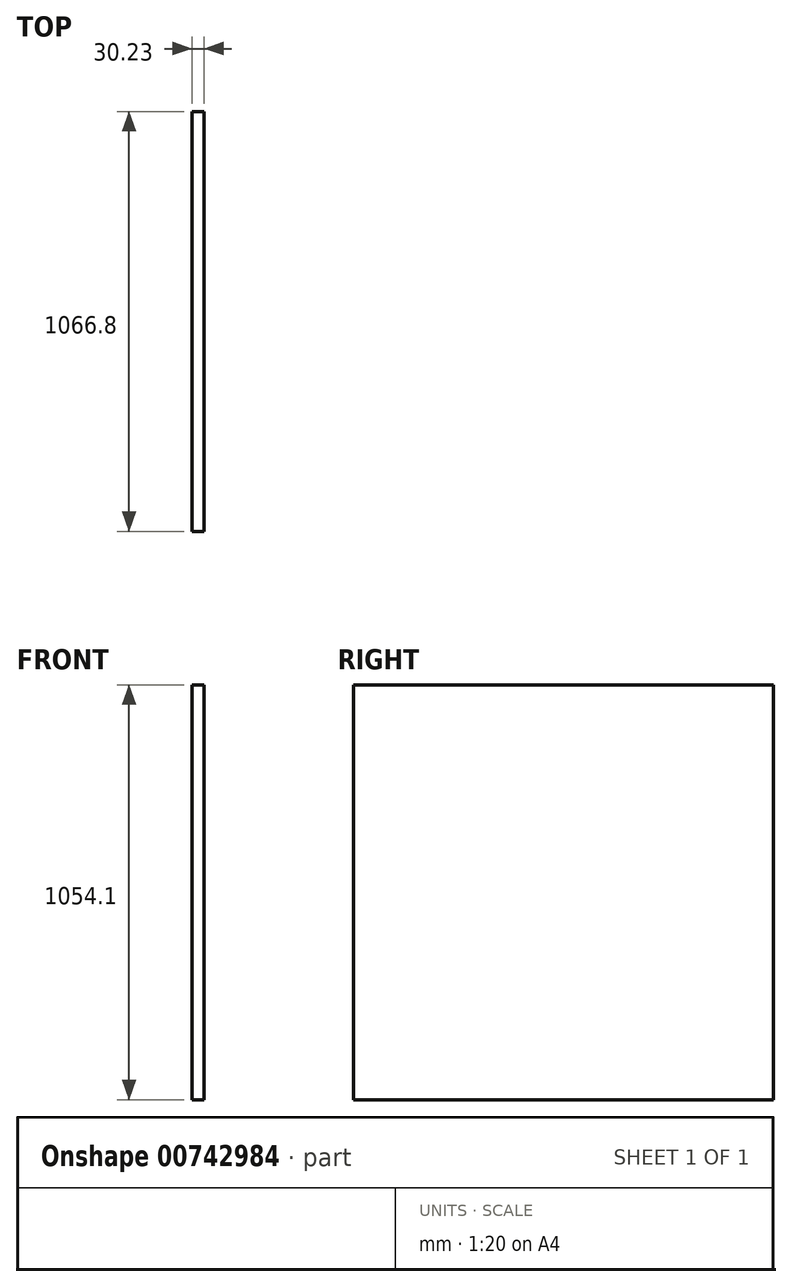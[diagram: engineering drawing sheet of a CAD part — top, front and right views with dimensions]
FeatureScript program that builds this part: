
annotation { "Feature Type Name" : "Feature", "Feature Type Description" : "" }
export const myFeature = defineFeature(function(context is Context, id is Id, definition is map)
    precondition{}
    {
        {
            var Q0;
            Q0=qCreatedBy(makeId("Right.planeOp"),FACE);
            var sketch = newSketch(context, id + "F0", { "sketchPlane" : qUnion([Q0])});
            skLineSegment(sketch, "E0.bottom", {"start": v(533.4, 527.05) * mm, "end": v(-533.4, 527.05) * mm});
            skLineSegment(sketch, "E0.top", {"start": v(533.4, -527.05) * mm, "end": v(-533.4, -527.05) * mm});
            skLineSegment(sketch, "E0.left", {"start": v(533.4, 527.05) * mm, "end": v(533.4, -527.05) * mm});
            skLineSegment(sketch, "E0.right", {"start": v(-533.4, 527.05) * mm, "end": v(-533.4, -527.05) * mm});
            skPoint(sketch, "E0.middle", {"position": v(0, 0) * mm});
            skSolve(sketch);
        }
        {
            var Q0;
            Q0=makeQuery(id+"F0.imprint","IMPRINT",FACE,{"disambiguationData":[TD([[makeQuery(id+"F0.imprint","IMPRINT",EDGE,{"derivedFrom":sQuery(id+"F0.wireOp",EDGE,"E0.bottom")}),1.0]])]});
            extrude(context, id + "F1", {"entities" : qUnion([Q0]), "depth" : 30.23 * mm, "offsetDistance" : 25.4 * mm});
        }
    });
